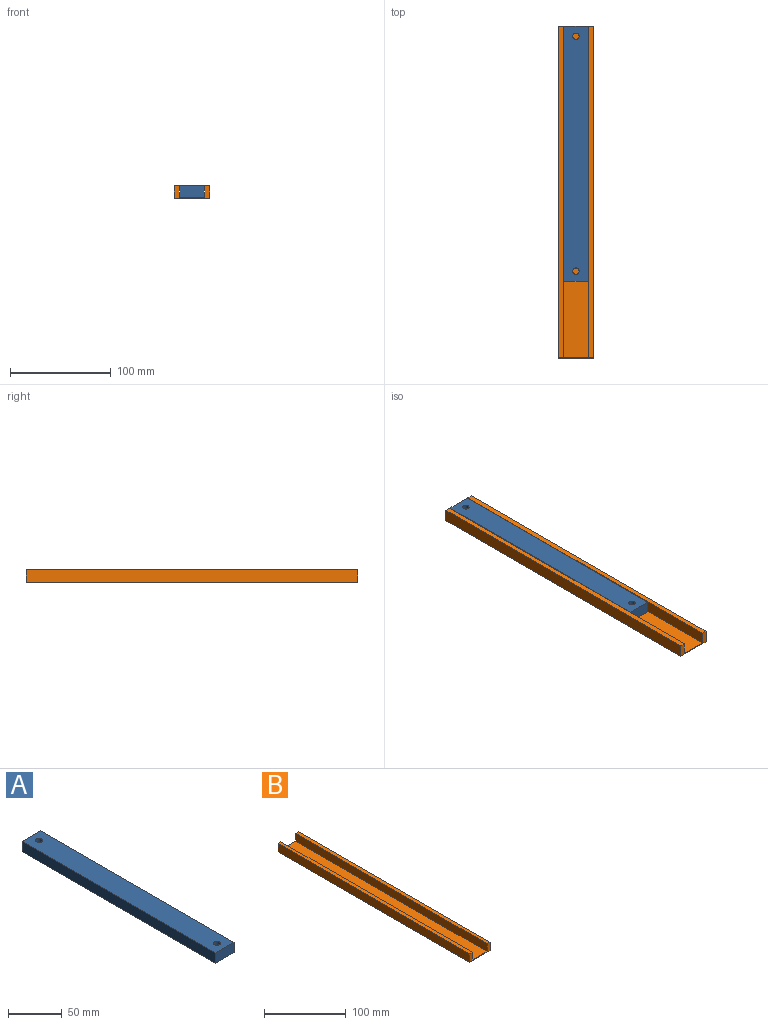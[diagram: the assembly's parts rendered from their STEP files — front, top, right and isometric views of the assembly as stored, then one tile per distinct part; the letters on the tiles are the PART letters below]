
ASSEMBLY  parts=2 mates=1
PART A: 8 faces, bbox 24.4x254x11.7 mm
  f0: plane 254x11.68mm, normal (-1,0,0), area 2967.7mm2, adj f1,f4,f6,f7
  f1: plane 24.38x11.68mm, normal (0,-1,0), area 284.9mm2, adj f0,f2,f6,f7
  f2: plane 254x11.68mm, normal (1,0,0), area 2967.7mm2, adj f1,f4,f6,f7
  f3: cylinder r=3.17mm len=11.68mm, axis (0,0,-1), area 233.1mm2, adj f6,f7
  f4: plane 24.38x11.68mm, normal (0,1,0), area 284.9mm2, adj f0,f2,f6,f7
  f5: cylinder r=3.17mm len=11.68mm, axis (0,0,-1), area 233.1mm2, adj f6,f7
  f6: plane 254x24.38mm, normal (0,0,1), area 6130.2mm2, adj f0,f1,f2,f3,f4,f5
  f7: plane 254x24.38mm, normal (0,0,-1), area 6130.2mm2, adj f0,f1,f2,f3,f4,f5
PART B: 10 faces, bbox 35.6x330.2x12.7 mm
  f0: plane 330.2x25.4mm, normal (0,0,1), area 8387.1mm2, adj f1,f3,f6,f8
  f1: plane 35.56x12.7mm, normal (0,-1,0), area 154.8mm2, adj f0,f2,f4,f5,f6,f7,f8,f9
  f2: plane 330.2x12.7mm, normal (1,0,0), area 4193.5mm2, adj f1,f3,f5,f9
  f3: plane 35.56x12.7mm, normal (0,1,0), area 154.8mm2, adj f0,f2,f4,f5,f6,f7,f8,f9
  f4: plane 330.2x12.7mm, normal (-1,0,0), area 4193.5mm2, adj f1,f3,f5,f7
  f5: plane 330.2x35.56mm, normal (0,0,-1), area 11741.9mm2, adj f1,f2,f3,f4
  f6: plane 330.2x11.68mm, normal (1,0,0), area 3858.1mm2, adj f0,f1,f3,f7
  f7: plane 330.2x5.08mm, normal (0,0,1), area 1677.4mm2, adj f1,f3,f4,f6
  f8: plane 330.2x11.68mm, normal (-1,0,0), area 3858.1mm2, adj f0,f1,f3,f9
  f9: plane 330.2x5.08mm, normal (0,0,1), area 1677.4mm2, adj f1,f2,f3,f8
PLACE A t=(8.73,-54.77,1.02)mm
PLACE B t=(24.89,-79.94,0)mm
MATE slider A.f4 <-> B.f3  axis (0,1,0) through (0,165.1,1.02)mm
